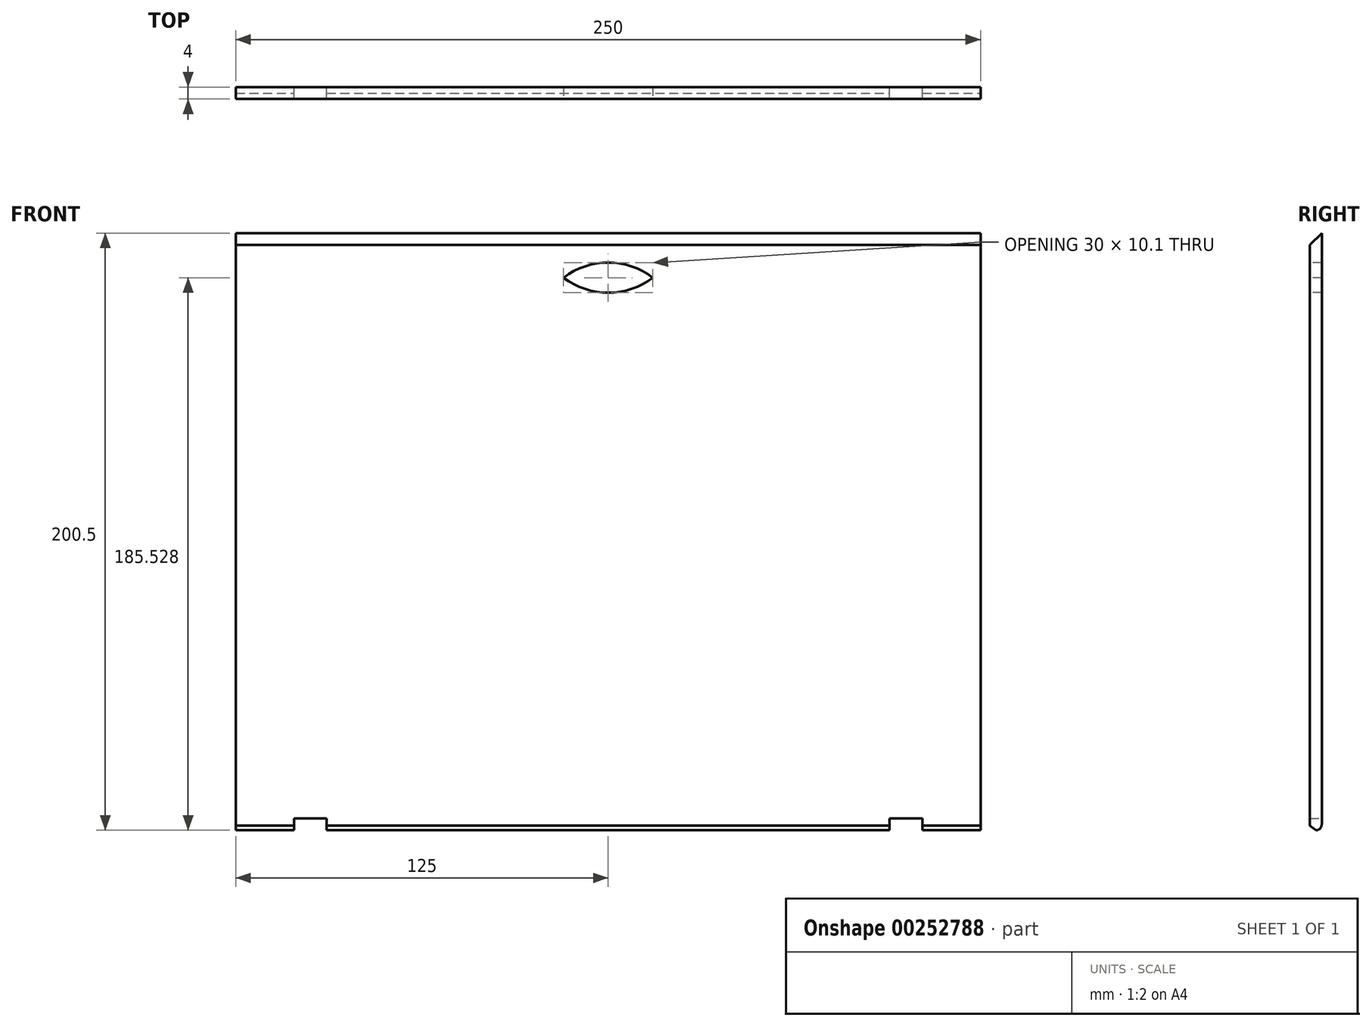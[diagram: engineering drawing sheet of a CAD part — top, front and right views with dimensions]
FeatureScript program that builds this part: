
annotation { "Feature Type Name" : "Feature", "Feature Type Description" : "" }
export const myFeature = defineFeature(function(context is Context, id is Id, definition is map)
    precondition{}
    {
        {
            var Q0;
            Q0=qCreatedBy(makeId("Front.planeOp"),FACE);
            var sketch = newSketch(context, id + "F0", { "sketchPlane" : qUnion([Q0])});
            skLineSegment(sketch, "E0.bottom", {"start": v(-125, 98.5) * mm, "end": v(125, 98.5) * mm});
            skLineSegment(sketch, "E0.top", {"start": v(-125, -98.5) * mm, "end": v(125, -98.5) * mm});
            skLineSegment(sketch, "E0.left", {"start": v(-125, 98.5) * mm, "end": v(-125, -98.5) * mm});
            skLineSegment(sketch, "E0.right", {"start": v(125, 98.5) * mm, "end": v(125, -98.5) * mm});
            skPoint(sketch, "E0.middle", {"position": v(0, 0) * mm});
            skSolve(sketch);
        }
        {
            var Q0;
            Q0 = qSketchRegion(id + "F0", true);
            extrude(context, id + "F1", {"entities" : qUnion([Q0]), "depth" : 4 * mm});
        }
        {
            var Q0;
            Q0=makeQuery(id+"F1.opExtrude","SWEPT_FACE",FACE,{"disambiguationData":[OSD([sQuery(id+"F0.wireOp",EDGE,"E0.right")])]});
            var sketch = newSketch(context, id + "F2", { "sketchPlane" : qUnion([Q0])});
            skLineSegment(sketch, "E1", {"start": v(-4, -98.5) * mm, "end": v(-4, -100) * mm});
            skLineSegment(sketch, "E2", {"start": v(-4, -100) * mm, "end": v(0, -100) * mm});
            skLineSegment(sketch, "E3", {"start": v(0, -100) * mm, "end": v(0, -98.5) * mm});
            skCircle(sketch, "E4", {"center": v(-2, -100) * mm, "radius": 2 * mm});
            skLineSegment(sketch, "E5", {"start": v(-2, -102) * mm, "end": v(-3.95, -100.44) * mm});
            skSolve(sketch);
        }
        {
            var Q0;
            Q0=makeQuery(id+"F1.opExtrude","SWEPT_FACE",FACE,{"disambiguationData":[OSD([sQuery(id+"F0.wireOp",EDGE,"E0.top")])]});
            var sketch = newSketch(context, id + "F3", { "sketchPlane" : qUnion([Q0])});
            skLineSegment(sketch, "E6.bottom", {"start": v(5.5, 0) * mm, "end": v(-5.5, 0) * mm});
            skLineSegment(sketch, "E6.top", {"start": v(5.5, 4) * mm, "end": v(-5.5, 4) * mm});
            skLineSegment(sketch, "E6.left", {"start": v(5.5, 0) * mm, "end": v(5.5, 4) * mm});
            skLineSegment(sketch, "E6.right", {"start": v(-5.5, 0) * mm, "end": v(-5.5, 4) * mm});
            skPoint(sketch, "E6.middle", {"position": v(0, 2) * mm});
            skPoint(sketch, "E6.middle.positionSnap0", {"position": v(-125, 2) * mm});
            skPoint(sketch, "E6.centerSnap0", {"position": v(-125, 2) * mm});
            skLineSegment(sketch, "E7", {"start": v(-125, 2) * mm, "end": v(-100, 2) * mm});
            skLineSegment(sketch, "E8.bottom", {"start": v(-105.5, 4) * mm, "end": v(-94.5, 4) * mm});
            skLineSegment(sketch, "E8.top", {"start": v(-105.5, 0) * mm, "end": v(-94.5, 0) * mm});
            skLineSegment(sketch, "E8.left", {"start": v(-105.5, 4) * mm, "end": v(-105.5, 0) * mm});
            skLineSegment(sketch, "E8.right", {"start": v(-94.5, 4) * mm, "end": v(-94.5, 0) * mm});
            skPoint(sketch, "E8.middle", {"position": v(-100, 2) * mm});
            skLineSegment(sketch, "E9.MirrorCS", {"start": v(94.5, 4) * mm, "end": v(94.5, 0) * mm});
            skLineSegment(sketch, "E10.MirrorCS", {"start": v(105.5, 4) * mm, "end": v(105.5, 0) * mm});
            skLineSegment(sketch, "E11.MirrorCS", {"start": v(105.5, 4) * mm, "end": v(94.5, 4) * mm});
            skLineSegment(sketch, "E12.MirrorCS", {"start": v(105.5, 0) * mm, "end": v(94.5, 0) * mm});
            skSolve(sketch);
        }
        {
            var Q0;
            {var subQ4=sQuery(id+"F3.wireOp",EDGE,"E8.bottom");Q0=makeQuery(id+"F3.imprint","IMPRINT",FACE,{"disambiguationData":[TD([[makeQuery(id+"F3.imprint","IMPRINT",EDGE,{"derivedFrom":subQ4}),-1.0]])]});}
            var Q1;
            Q1=makeQuery(id+"F3.imprint","IMPRINT",FACE,{"disambiguationData":[TD([[makeQuery(id+"F3.imprint","IMPRINT",EDGE,{"derivedFrom":sQuery(id+"F3.wireOp",EDGE,"E9.MirrorCS")}),1.0]])]});
            extrude(context, id + "F4", {"entities" : qUnion([Q0, Q1]), "operationType" : NewBodyOperationType.REMOVE, "oppositeDirection" : true, "depth" : 0.5 * mm});
        }
        {
            var Q0;
            {var subQ1=sQuery(id+"F0.wireOp",EDGE,"E0.right");var subQ2=makeQuery(id+"F1.opExtrude","SWEPT_EDGE",EDGE,{"disambiguationData":[OSD([sQuery(id+"F0.wireOp",EDGE,"E0.top"),subQ1])]});Q0=makeQuery(id+"F2.imprint","IMPRINT",FACE,{"disambiguationData":[TD([[makeQuery(id+"F2.imprint","IMPRINT",EDGE,{"derivedFrom":subQ2}),-1.0]])]});}
            var Q1;
            {var subQ0=sQuery(id+"F2.wireOp",EDGE,"E2");Q1=makeQuery(id+"F2.imprint","IMPRINT",FACE,{"disambiguationData":[TD([[makeQuery(id+"F2.imprint","IMPRINT",EDGE,{"derivedFrom":subQ0}),1.0]])]});}
            var Q2;
            {var subQ0=sQuery(id+"F2.wireOp",EDGE,"E2");Q2=makeQuery(id+"F2.imprint","IMPRINT",FACE,{"disambiguationData":[TD([[makeQuery(id+"F2.imprint","IMPRINT",EDGE,{"derivedFrom":subQ0}),-1.0]])]});}
            extrude(context, id + "F5", {"entities" : qUnion([Q0, Q1, Q2]), "operationType" : NewBodyOperationType.ADD, "oppositeDirection" : true, "depth" : 250 * mm});
        }
        {
            var Q0;
            {var subQ4=sQuery(id+"F3.wireOp",EDGE,"E8.bottom");Q0=makeQuery(id+"F3.imprint","IMPRINT",FACE,{"disambiguationData":[TD([[makeQuery(id+"F3.imprint","IMPRINT",EDGE,{"derivedFrom":subQ4}),-1.0]])]});}
            var Q1;
            Q1=makeQuery(id+"F3.imprint","IMPRINT",FACE,{"disambiguationData":[TD([[makeQuery(id+"F3.imprint","IMPRINT",EDGE,{"derivedFrom":sQuery(id+"F3.wireOp",EDGE,"E9.MirrorCS")}),1.0]])]});
            extrude(context, id + "F6", {"entities" : qUnion([Q0, Q1]), "operationType" : NewBodyOperationType.REMOVE, "depth" : 25 * mm});
        }
        {
            var Q0;
            Q0=makeQuery(id+"F5.boolean.opBoolean","MERGE",FACE,{"derivedFrom":[makeQuery(id+"F1.opExtrude","CAP_FACE",FACE,{"disambiguationData":[OSD([sQuery(id+"F0.wireOp",EDGE,"E0.bottom"),sQuery(id+"F0.wireOp",EDGE,"E0.top"),sQuery(id+"F0.wireOp",EDGE,"E0.left"),sQuery(id+"F0.wireOp",EDGE,"E0.right")])],"isStart":false}),makeQuery(id+"F5.opExtrude","SWEPT_FACE",FACE,{"disambiguationData":[OSD([sQuery(id+"F2.wireOp",EDGE,"E1")])]})]});
            var sketch = newSketch(context, id + "F7", { "sketchPlane" : qUnion([Q0])});
            skLineSegment(sketch, "E13", {"start": v(0, 98.5) * mm, "end": v(0, 83.5) * mm});
            skPoint(sketch, "E13.endSnap0", {"position": v(0, 98.5) * mm});
            skCircle(sketch, "E14", {"center": v(0, 83.5) * mm, "radius": 5 * mm});
            skLineSegment(sketch, "E15", {"start": v(0, 83.5) * mm, "end": v(15, 83.5) * mm});
            skLineSegment(sketch, "E16", {"start": v(0, 83.5) * mm, "end": v(-15, 83.5) * mm});
            skArc(sketch, "E17", {"start": v(15, 83.5) * mm, "mid": v(0, 88.58) * mm, "end": v(-15, 83.5) * mm});
            skArc(sketch, "E18", {"start": v(-15, 83.5) * mm, "mid": v(0, 78.48) * mm, "end": v(15, 83.5) * mm});
            skSolve(sketch);
        }
        {
            var Q0;
            {var subQ5=sQuery(id+"F7.wireOp",EDGE,"E18");Q0=makeQuery(id+"F7.imprint","IMPRINT",FACE,{"disambiguationData":[TD([[makeQuery(id+"F7.imprint","IMPRINT",EDGE,{"derivedFrom":subQ5}),1.0]])]});}
            var Q1;
            {var subQ0=sQuery(id+"F7.wireOp",EDGE,"E15");var subQ1=sQuery(id+"F7.wireOp",EDGE,"E14");var subQ2=makeQuery(id+"F7.imprint","INTERSECT",VERTEX,{"derivedFrom":[subQ1,subQ0]});Q1=makeQuery(id+"F7.imprint","IMPRINT",FACE,{"disambiguationData":[TD([[makeQuery(id+"F7.imprint","IMPRINT",EDGE,{"disambiguationData":[TD([[subQ2,1.0]])],"derivedFrom":subQ1}),1.0]])]});}
            var Q2;
            {var subQ1=sQuery(id+"F7.wireOp",EDGE,"E13");var subQ3=sQuery(id+"F7.wireOp",EDGE,"E14");var subQ4=makeQuery(id+"F7.imprint","INTERSECT",VERTEX,{"derivedFrom":[subQ1,subQ3]});Q2=makeQuery(id+"F7.imprint","IMPRINT",FACE,{"disambiguationData":[TD([[makeQuery(id+"F7.imprint","IMPRINT",EDGE,{"disambiguationData":[TD([[subQ4,-1.0]])],"derivedFrom":subQ3}),1.0]])]});}
            var Q3;
            {var subQ0=sQuery(id+"F7.wireOp",EDGE,"E17");var subQ1=sQuery(id+"F7.wireOp",EDGE,"E13");var subQ2=makeQuery(id+"F7.imprint","INTERSECT",VERTEX,{"derivedFrom":[subQ1,subQ0]});Q3=makeQuery(id+"F7.imprint","IMPRINT",FACE,{"disambiguationData":[TD([[makeQuery(id+"F7.imprint","IMPRINT",EDGE,{"disambiguationData":[TD([[subQ2,-1.0]])],"derivedFrom":subQ1}),-1.0]])]});}
            var Q4;
            {var subQ1=sQuery(id+"F7.wireOp",EDGE,"E13");var subQ3=sQuery(id+"F7.wireOp",EDGE,"E14");var subQ4=makeQuery(id+"F7.imprint","INTERSECT",VERTEX,{"derivedFrom":[subQ1,subQ3]});Q4=makeQuery(id+"F7.imprint","IMPRINT",FACE,{"disambiguationData":[TD([[makeQuery(id+"F7.imprint","IMPRINT",EDGE,{"disambiguationData":[TD([[subQ4,1.0]])],"derivedFrom":subQ3}),1.0]])]});}
            var Q5;
            {var subQ0=sQuery(id+"F7.wireOp",EDGE,"E17");var subQ1=sQuery(id+"F7.wireOp",EDGE,"E13");var subQ2=makeQuery(id+"F7.imprint","INTERSECT",VERTEX,{"derivedFrom":[subQ1,subQ0]});Q5=makeQuery(id+"F7.imprint","IMPRINT",FACE,{"disambiguationData":[TD([[makeQuery(id+"F7.imprint","IMPRINT",EDGE,{"disambiguationData":[TD([[subQ2,-1.0]])],"derivedFrom":subQ1}),1.0]])]});}
            extrude(context, id + "F8", {"entities" : qUnion([Q0, Q1, Q2, Q3, Q4, Q5]), "operationType" : NewBodyOperationType.REMOVE, "oppositeDirection" : true, "depth" : 25 * mm});
        }
        {
            var Q0;
            Q0=makeQuery(id+"F1.opExtrude","CAP_EDGE",EDGE,{"disambiguationData":[OSD([sQuery(id+"F0.wireOp",EDGE,"E0.bottom")])],"isStart":false});
            chamfer(context, id + "F9", {"entities" : qUnion([Q0]), "width" : 4 * mm, "tangentPropagation" : true});
        }
    });
